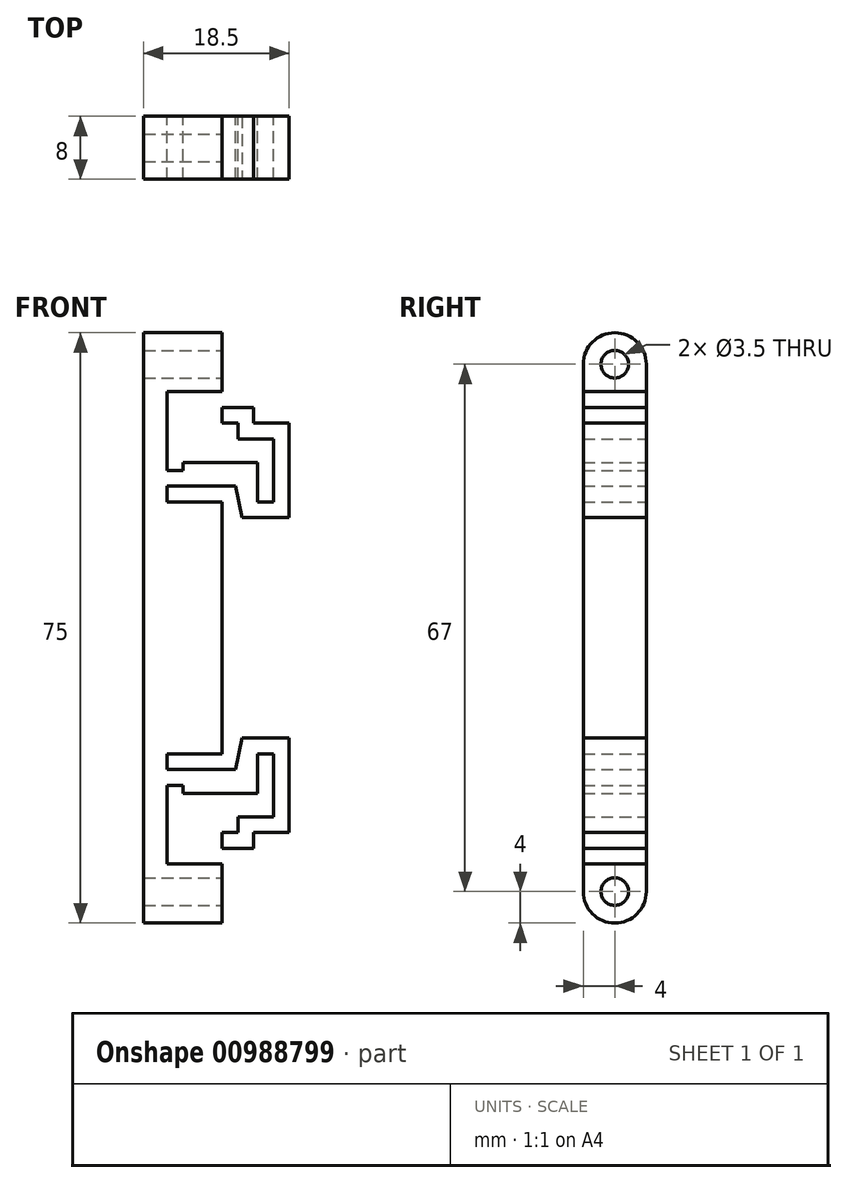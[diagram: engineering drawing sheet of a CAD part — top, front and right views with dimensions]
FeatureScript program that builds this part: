
annotation { "Feature Type Name" : "Feature", "Feature Type Description" : "" }
export const myFeature = defineFeature(function(context is Context, id is Id, definition is map)
    precondition{}
    {
        {
            var Q0;
            Q0=qCreatedBy(makeId("Front.planeOp"),FACE);
            var sketch = newSketch(context, id + "F0", { "sketchPlane" : qUnion([Q0])});
            skLineSegment(sketch, "E0.bottom", {"start": v(0, 0) * mm, "end": v(10, 0) * mm});
            skLineSegment(sketch, "E0.top", {"start": v(0, 75) * mm, "end": v(10, 75) * mm});
            skLineSegment(sketch, "E0.left", {"start": v(0, 0) * mm, "end": v(0, 75) * mm});
            skLineSegment(sketch, "E0.right", {"start": v(10, 0) * mm, "end": v(10, 75) * mm});
            skLineSegment(sketch, "E1", {"start": v(0, 37.5) * mm, "end": v(10, 37.5) * mm, "construction": true});
            skLineSegment(sketch, "E2.bottom", {"start": v(10, 55.5) * mm, "end": v(11.5, 55.5) * mm});
            skLineSegment(sketch, "E2.top", {"start": v(10, 19.5) * mm, "end": v(11.5, 19.5) * mm});
            skLineSegment(sketch, "E2.left", {"start": v(10, 55.5) * mm, "end": v(10, 19.5) * mm});
            skLineSegment(sketch, "E2.right", {"start": v(11.5, 55.5) * mm, "end": v(11.5, 19.5) * mm});
            skLineSegment(sketch, "E3.bottom", {"start": v(11.5, 51.5) * mm, "end": v(18.5, 51.5) * mm});
            skLineSegment(sketch, "E3.top", {"start": v(11.5, 23.5) * mm, "end": v(18.5, 23.5) * mm});
            skLineSegment(sketch, "E3.left", {"start": v(11.5, 51.5) * mm, "end": v(11.5, 23.5) * mm});
            skLineSegment(sketch, "E3.right", {"start": v(18.5, 51.5) * mm, "end": v(18.5, 23.5) * mm});
            skLineSegment(sketch, "E4.bottom", {"start": v(10, 75) * mm, "end": v(18.5, 75) * mm});
            skLineSegment(sketch, "E4.top", {"start": v(10, 0) * mm, "end": v(18.5, 0) * mm});
            skLineSegment(sketch, "E4.left", {"start": v(10, 75) * mm, "end": v(10, 0) * mm});
            skLineSegment(sketch, "E4.right", {"start": v(18.5, 75) * mm, "end": v(18.5, 0) * mm});
            skLineSegment(sketch, "E5.bottom", {"start": v(3, 61.5) * mm, "end": v(16.5, 61.5) * mm});
            skLineSegment(sketch, "E5.top", {"start": v(3, 58.5) * mm, "end": v(16.5, 58.5) * mm});
            skLineSegment(sketch, "E5.left", {"start": v(3, 61.5) * mm, "end": v(3, 58.5) * mm});
            skLineSegment(sketch, "E5.right", {"start": v(16.5, 61.5) * mm, "end": v(16.5, 58.5) * mm});
            skLineSegment(sketch, "E6.bottom", {"start": v(18.5, 75) * mm, "end": v(10, 75) * mm});
            skLineSegment(sketch, "E6.top", {"start": v(18.5, 65.5) * mm, "end": v(10, 65.5) * mm});
            skLineSegment(sketch, "E6.left", {"start": v(18.5, 75) * mm, "end": v(18.5, 65.5) * mm});
            skLineSegment(sketch, "E6.right", {"start": v(10, 75) * mm, "end": v(10, 65.5) * mm});
            skLineSegment(sketch, "E7.top", {"start": v(10, 9.5) * mm, "end": v(18.5, 9.5) * mm});
            skLineSegment(sketch, "E7.left", {"start": v(10, 0) * mm, "end": v(10, 9.5) * mm});
            skLineSegment(sketch, "E7.right", {"start": v(18.5, 0) * mm, "end": v(18.5, 9.5) * mm});
            skLineSegment(sketch, "E8.bottom", {"start": v(3, 16.5) * mm, "end": v(16.5, 16.5) * mm});
            skLineSegment(sketch, "E8.top", {"start": v(3, 13.5) * mm, "end": v(16.5, 13.5) * mm});
            skLineSegment(sketch, "E8.left", {"start": v(3, 16.5) * mm, "end": v(3, 13.5) * mm});
            skLineSegment(sketch, "E8.right", {"start": v(16.5, 16.5) * mm, "end": v(16.5, 13.5) * mm});
            skLineSegment(sketch, "E9.bottom", {"start": v(10, 13.5) * mm, "end": v(12, 13.5) * mm});
            skLineSegment(sketch, "E9.top", {"start": v(10, 11.5) * mm, "end": v(12, 11.5) * mm});
            skLineSegment(sketch, "E9.left", {"start": v(10, 13.5) * mm, "end": v(10, 11.5) * mm});
            skLineSegment(sketch, "E9.right", {"start": v(12, 13.5) * mm, "end": v(12, 11.5) * mm});
            skLineSegment(sketch, "E10.bottom", {"start": v(14, 9.5) * mm, "end": v(18.5, 9.5) * mm});
            skLineSegment(sketch, "E10.top", {"start": v(14, 11.5) * mm, "end": v(18.5, 11.5) * mm});
            skLineSegment(sketch, "E10.left", {"start": v(14, 9.5) * mm, "end": v(14, 11.5) * mm});
            skLineSegment(sketch, "E10.right", {"start": v(18.5, 9.5) * mm, "end": v(18.5, 11.5) * mm});
            skLineSegment(sketch, "E11.bottom", {"start": v(10, 61.5) * mm, "end": v(12, 61.5) * mm});
            skLineSegment(sketch, "E11.top", {"start": v(10, 63.5) * mm, "end": v(12, 63.5) * mm});
            skLineSegment(sketch, "E11.left", {"start": v(10, 61.5) * mm, "end": v(10, 63.5) * mm});
            skLineSegment(sketch, "E11.right", {"start": v(12, 61.5) * mm, "end": v(12, 63.5) * mm});
            skLineSegment(sketch, "E12.bottom", {"start": v(14, 65.5) * mm, "end": v(18.5, 65.5) * mm});
            skLineSegment(sketch, "E12.top", {"start": v(14, 63.5) * mm, "end": v(18.5, 63.5) * mm});
            skLineSegment(sketch, "E12.left", {"start": v(14, 65.5) * mm, "end": v(14, 63.5) * mm});
            skLineSegment(sketch, "E12.right", {"start": v(18.5, 65.5) * mm, "end": v(18.5, 63.5) * mm});
            skLineSegment(sketch, "E13.bottom", {"start": v(16.5, 58.5) * mm, "end": v(14.5, 58.5) * mm});
            skLineSegment(sketch, "E13.top", {"start": v(16.5, 53.5) * mm, "end": v(14.5, 53.5) * mm});
            skLineSegment(sketch, "E13.left", {"start": v(16.5, 58.5) * mm, "end": v(16.5, 53.5) * mm});
            skLineSegment(sketch, "E13.right", {"start": v(14.5, 58.5) * mm, "end": v(14.5, 53.5) * mm});
            skLineSegment(sketch, "E14.bottom", {"start": v(16.5, 16.5) * mm, "end": v(14.5, 16.5) * mm});
            skLineSegment(sketch, "E14.top", {"start": v(16.5, 21.5) * mm, "end": v(14.5, 21.5) * mm});
            skLineSegment(sketch, "E14.left", {"start": v(16.5, 16.5) * mm, "end": v(16.5, 21.5) * mm});
            skLineSegment(sketch, "E14.right", {"start": v(14.5, 16.5) * mm, "end": v(14.5, 21.5) * mm});
            skLineSegment(sketch, "E15.bottom", {"start": v(10, 19.5) * mm, "end": v(3, 19.5) * mm});
            skLineSegment(sketch, "E15.top", {"start": v(10, 21.5) * mm, "end": v(3, 21.5) * mm});
            skLineSegment(sketch, "E15.left", {"start": v(10, 19.5) * mm, "end": v(10, 21.5) * mm});
            skLineSegment(sketch, "E15.right", {"start": v(3, 19.5) * mm, "end": v(3, 21.5) * mm});
            skLineSegment(sketch, "E16.bottom", {"start": v(10, 55.5) * mm, "end": v(3, 55.5) * mm});
            skLineSegment(sketch, "E16.top", {"start": v(10, 53.5) * mm, "end": v(3, 53.5) * mm});
            skLineSegment(sketch, "E16.left", {"start": v(10, 55.5) * mm, "end": v(10, 53.5) * mm});
            skLineSegment(sketch, "E16.right", {"start": v(3, 55.5) * mm, "end": v(3, 53.5) * mm});
            skLineSegment(sketch, "E17.bottom", {"start": v(10, 65.5) * mm, "end": v(3, 65.5) * mm});
            skLineSegment(sketch, "E17.top", {"start": v(10, 67.5) * mm, "end": v(3, 67.5) * mm});
            skLineSegment(sketch, "E17.left", {"start": v(10, 65.5) * mm, "end": v(10, 67.5) * mm});
            skLineSegment(sketch, "E17.right", {"start": v(3, 65.5) * mm, "end": v(3, 67.5) * mm});
            skLineSegment(sketch, "E18.bottom", {"start": v(10, 9.5) * mm, "end": v(3, 9.5) * mm});
            skLineSegment(sketch, "E18.top", {"start": v(10, 7.5) * mm, "end": v(3, 7.5) * mm});
            skLineSegment(sketch, "E18.left", {"start": v(10, 9.5) * mm, "end": v(10, 7.5) * mm});
            skLineSegment(sketch, "E18.right", {"start": v(3, 9.5) * mm, "end": v(3, 7.5) * mm});
            skLineSegment(sketch, "E19.bottom", {"start": v(6, 65.5) * mm, "end": v(8, 65.5) * mm});
            skLineSegment(sketch, "E19.top", {"start": v(6, 63.5) * mm, "end": v(8, 63.5) * mm});
            skLineSegment(sketch, "E19.left", {"start": v(6, 65.5) * mm, "end": v(6, 63.5) * mm});
            skLineSegment(sketch, "E19.right", {"start": v(8, 65.5) * mm, "end": v(8, 63.5) * mm});
            skLineSegment(sketch, "E20.bottom", {"start": v(6, 9.5) * mm, "end": v(8, 9.5) * mm});
            skLineSegment(sketch, "E20.top", {"start": v(6, 11.5) * mm, "end": v(8, 11.5) * mm});
            skLineSegment(sketch, "E20.left", {"start": v(6, 9.5) * mm, "end": v(6, 11.5) * mm});
            skLineSegment(sketch, "E20.right", {"start": v(8, 9.5) * mm, "end": v(8, 11.5) * mm});
            skLineSegment(sketch, "E21", {"start": v(3, 65.5) * mm, "end": v(3, 61.5) * mm});
            skLineSegment(sketch, "E22", {"start": v(3, 13.5) * mm, "end": v(3, 9.5) * mm});
            skLineSegment(sketch, "E23.bottom", {"start": v(3, 16.5) * mm, "end": v(5, 16.5) * mm});
            skLineSegment(sketch, "E23.top", {"start": v(3, 17.5) * mm, "end": v(5, 17.5) * mm});
            skLineSegment(sketch, "E23.left", {"start": v(3, 16.5) * mm, "end": v(3, 17.5) * mm});
            skLineSegment(sketch, "E23.right", {"start": v(5, 16.5) * mm, "end": v(5, 17.5) * mm});
            skLineSegment(sketch, "E24.bottom", {"start": v(3, 58.5) * mm, "end": v(5, 58.5) * mm});
            skLineSegment(sketch, "E24.top", {"start": v(3, 57.5) * mm, "end": v(5, 57.5) * mm});
            skLineSegment(sketch, "E24.left", {"start": v(3, 58.5) * mm, "end": v(3, 57.5) * mm});
            skLineSegment(sketch, "E24.right", {"start": v(5, 58.5) * mm, "end": v(5, 57.5) * mm});
            skSolve(sketch);
        }
        {
            var Q0;
            {var subQ5=sQuery(id+"F0.wireOp",EDGE,"E2.bottom");Q0=makeQuery(id+"F0.imprint","IMPRINT",FACE,{"disambiguationData":[TD([[makeQuery(id+"F0.imprint","IMPRINT",EDGE,{"derivedFrom":subQ5}),1.0]])]});}
            var Q1;
            {var subQ13=sQuery(id+"F0.wireOp",EDGE,"E2.top");Q1=makeQuery(id+"F0.imprint","IMPRINT",FACE,{"disambiguationData":[TD([[makeQuery(id+"F0.imprint","IMPRINT",EDGE,{"derivedFrom":subQ13}),-1.0]])]});}
            var Q2;
            {var subQ13=sQuery(id+"F0.wireOp",EDGE,"E0.bottom");Q2=makeQuery(id+"F0.imprint","IMPRINT",FACE,{"disambiguationData":[TD([[makeQuery(id+"F0.imprint","IMPRINT",EDGE,{"derivedFrom":subQ13}),1.0]])]});}
            extrude(context, id + "F1", {"entities" : qUnion([Q0, Q1, Q2]), "depth" : 8 * mm, "offsetDistance" : 25 * mm});
        }
        {
            var Q0;
            Q0=makeQuery(id+"F1.opExtrude","SWEPT_EDGE",EDGE,{"disambiguationData":[OSD([sQuery(id+"F0.wireOp",EDGE,"E2.right"),sQuery(id+"F0.wireOp",EDGE,"E3.bottom")])]});
            chamfer(context, id + "F2", {"entities" : qUnion([Q0]), "chamferType" : ChamferType.TWO_OFFSETS, "width1" : 1 * mm, "oppositeDirection" : false, "width2" : 5 * mm, "tangentPropagation" : true});
        }
        {
            var Q0;
            Q0=makeQuery(id+"F1.opExtrude","SWEPT_EDGE",EDGE,{"disambiguationData":[OSD([sQuery(id+"F0.wireOp",EDGE,"E2.right"),sQuery(id+"F0.wireOp",EDGE,"E3.top")])]});
            chamfer(context, id + "F3", {"entities" : qUnion([Q0]), "chamferType" : ChamferType.TWO_OFFSETS, "width1" : 5 * mm, "oppositeDirection" : false, "width2" : 1 * mm, "tangentPropagation" : true});
        }
        {
            var Q0;
            Q0=makeQuery(id+"F1.opExtrude","CAP_EDGE",EDGE,{"disambiguationData":[OSD([sQuery(id+"F0.wireOp",EDGE,"E0.top")])],"isStart":false});
            var Q1;
            Q1=makeQuery(id+"F1.opExtrude","CAP_EDGE",EDGE,{"disambiguationData":[OSD([sQuery(id+"F0.wireOp",EDGE,"E0.top")])],"isStart":true});
            var Q2;
            Q2=makeQuery(id+"F1.opExtrude","CAP_EDGE",EDGE,{"disambiguationData":[OSD([sQuery(id+"F0.wireOp",EDGE,"E0.bottom")])],"isStart":false});
            var Q3;
            Q3=makeQuery(id+"F1.opExtrude","CAP_EDGE",EDGE,{"disambiguationData":[OSD([sQuery(id+"F0.wireOp",EDGE,"E0.bottom")])],"isStart":true});
            fillet(context, id + "F4", {"entities" : qUnion([Q0, Q1, Q2, Q3]), "radius" : 4 * mm, "tangentPropagation" : true, "allowEdgeOverflow" : false});
        }
        {
            var Q0;
            {var subQ0=sQuery(id+"F0.wireOp",EDGE,"E0.right");Q0=makeQuery(id+"F1.opExtrude","SWEPT_FACE",FACE,{"disambiguationData":[OSD([subQ0]),TDD([makeQuery(id+"F0.imprint","IMPRINT",EDGE,{"disambiguationData":[TD([[makeQuery(id+"F0.imprint","INTERSECT",VERTEX,{"derivedFrom":[subQ0,sQuery(id+"F0.wireOp",EDGE,"E17.top")]}),-1.0]])],"derivedFrom":subQ0})])]});}
            var sketch = newSketch(context, id + "F5", { "sketchPlane" : qUnion([Q0])});
            skLineSegment(sketch, "E25", {"start": v(-8, 71) * mm, "end": v(0, 71) * mm, "construction": true});
            skCircle(sketch, "E26", {"center": v(-4, 71) * mm, "radius": 1.75 * mm});
            skSolve(sketch);
        }
        {
            var Q0;
            Q0=makeQuery(id+"F5.imprint","IMPRINT",FACE,{"disambiguationData":[TD([[makeQuery(id+"F5.imprint","IMPRINT",EDGE,{"derivedFrom":sQuery(id+"F5.wireOp",EDGE,"E26")}),1.0]])]});
            var Q1;
            Q1=sQuery(id+"F5.wireOp",EDGE,"E26");
            extrude(context, id + "F6", {"entities" : qUnion([Q0]), "operationType" : NewBodyOperationType.REMOVE, "surfaceEntities" : qUnion([Q1]), "oppositeDirection" : true, "depth" : 10 * mm, "offsetDistance" : 25 * mm});
        }
        {
            var Q0;
            {var subQ0=sQuery(id+"F0.wireOp",EDGE,"E0.right");Q0=makeQuery(id+"F1.opExtrude","SWEPT_FACE",FACE,{"disambiguationData":[OSD([subQ0]),TDD([makeQuery(id+"F0.imprint","IMPRINT",EDGE,{"disambiguationData":[TD([[makeQuery(id+"F0.imprint","INTERSECT",VERTEX,{"derivedFrom":[subQ0,sQuery(id+"F0.wireOp",EDGE,"E18.top")]}),1.0]])],"derivedFrom":subQ0})])]});}
            var sketch = newSketch(context, id + "F7", { "sketchPlane" : qUnion([Q0])});
            skLineSegment(sketch, "E27", {"start": v(0, 4) * mm, "end": v(-8, 4) * mm, "construction": true});
            skCircle(sketch, "E28", {"center": v(-4, 4) * mm, "radius": 1.75 * mm});
            skPoint(sketch, "E28.perimeterSnap0", {"position": v(-4, 4) * mm});
            skPoint(sketch, "E28.perimeterSnap1", {"position": v(-8, 5.75) * mm});
            skSolve(sketch);
        }
        {
            var Q0;
            Q0 = qSketchRegion(id + "F7", true);
            extrude(context, id + "F8", {"entities" : qUnion([Q0]), "operationType" : NewBodyOperationType.REMOVE, "oppositeDirection" : true, "depth" : 10 * mm, "offsetDistance" : 25 * mm});
        }
    });
